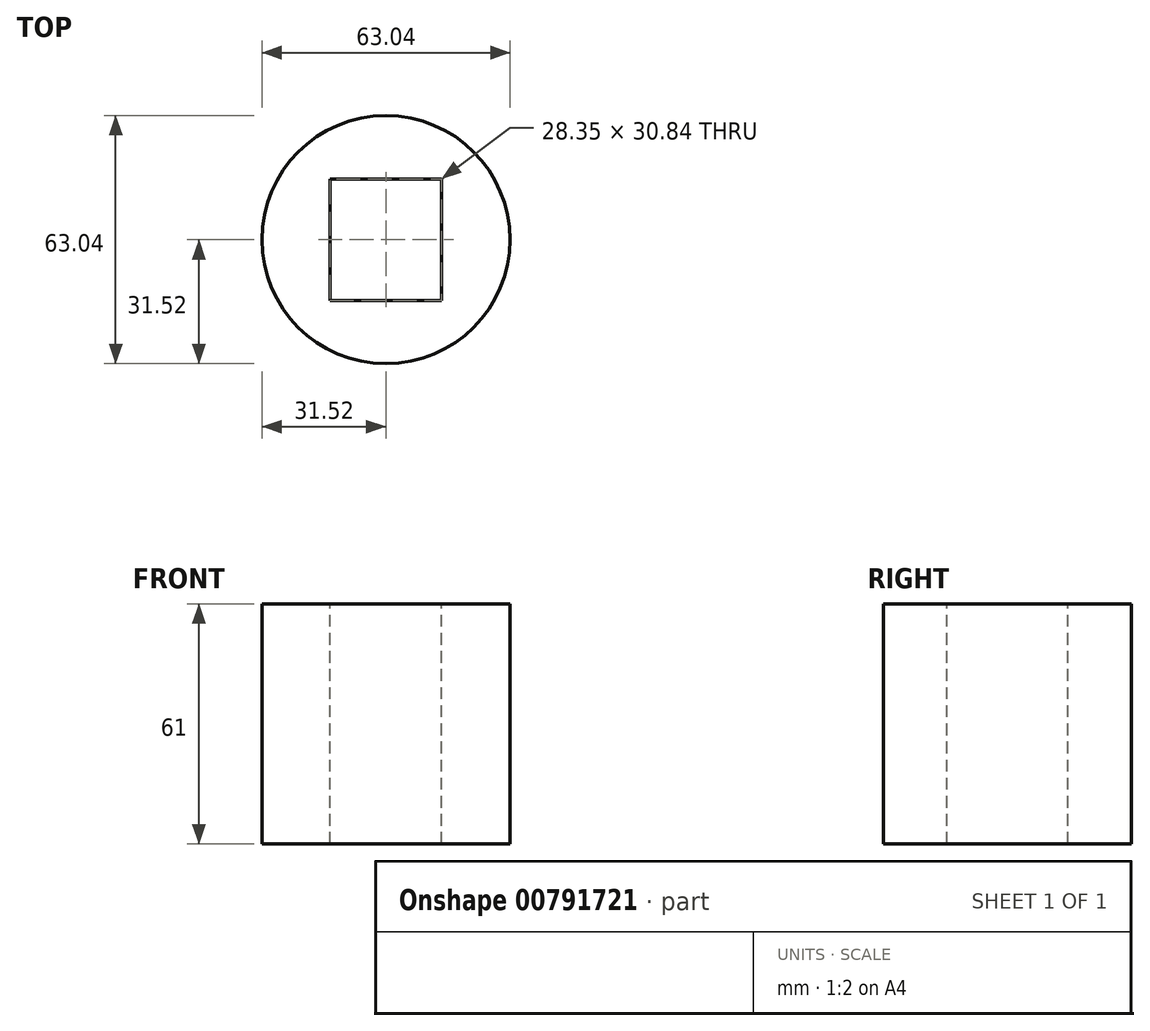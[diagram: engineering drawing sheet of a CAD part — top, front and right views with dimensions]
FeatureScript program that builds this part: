
annotation { "Feature Type Name" : "Feature", "Feature Type Description" : "" }
export const myFeature = defineFeature(function(context is Context, id is Id, definition is map)
    precondition{}
    {
        {
            var Q0;
            Q0=qCreatedBy(makeId("Top.planeOp"),FACE);
            var sketch = newSketch(context, id + "F0", { "sketchPlane" : qUnion([Q0])});
            skCircle(sketch, "E0", {"center": v(0, 0) * mm, "radius": 31.52 * mm});
            skSolve(sketch);
        }
        {
            var Q0;
            Q0 = qSketchRegion(id + "F0", true);
            extrude(context, id + "F1", {"entities" : qUnion([Q0]), "depth" : 25 * mm, "offsetDistance" : 25 * mm});
        }
        {
            var Q0;
            Q0=makeQuery(id+"F1.opExtrude","SWEPT_BODY",BODY,{"disambiguationData":[OSD([sQuery(id+"F0.wireOp",EDGE,"E0")])]});
            deleteBodies(context, id + "F2", {"entities" : qUnion([Q0])});
        }
        {
            var Q0;
            Q0=makeQuery(id+"F0.imprint","IMPRINT",FACE,{"disambiguationData":[TD([[makeQuery(id+"F0.imprint","IMPRINT",EDGE,{"derivedFrom":sQuery(id+"F0.wireOp",EDGE,"E0")}),1.0]])]});
            extrude(context, id + "F3", {"entities" : qUnion([Q0]), "depth" : 61 * mm, "offsetDistance" : 25 * mm});
        }
        {
            var Q0;
            Q0=makeQuery(id+"F3.opExtrude","CAP_FACE",FACE,{"disambiguationData":[OSD([sQuery(id+"F0.wireOp",EDGE,"E0")])],"isStart":false});
            var sketch = newSketch(context, id + "F4", { "sketchPlane" : qUnion([Q0])});
            skLineSegment(sketch, "E1.bottom", {"start": v(-14.17, -15.42) * mm, "end": v(14.17, -15.42) * mm});
            skLineSegment(sketch, "E1.top", {"start": v(-14.17, 15.42) * mm, "end": v(14.17, 15.42) * mm});
            skLineSegment(sketch, "E1.left", {"start": v(-14.17, -15.42) * mm, "end": v(-14.17, 15.42) * mm});
            skLineSegment(sketch, "E1.right", {"start": v(14.17, -15.42) * mm, "end": v(14.17, 15.42) * mm});
            skPoint(sketch, "E1.middle", {"position": v(0, 0) * mm});
            skSolve(sketch);
        }
        {
            var Q0;
            Q0 = qSketchRegion(id + "F4", true);
            extrude(context, id + "F5", {"entities" : qUnion([Q0]), "operationType" : NewBodyOperationType.REMOVE, "oppositeDirection" : true, "depth" : 75 * mm, "offsetDistance" : 25 * mm});
        }
    });
